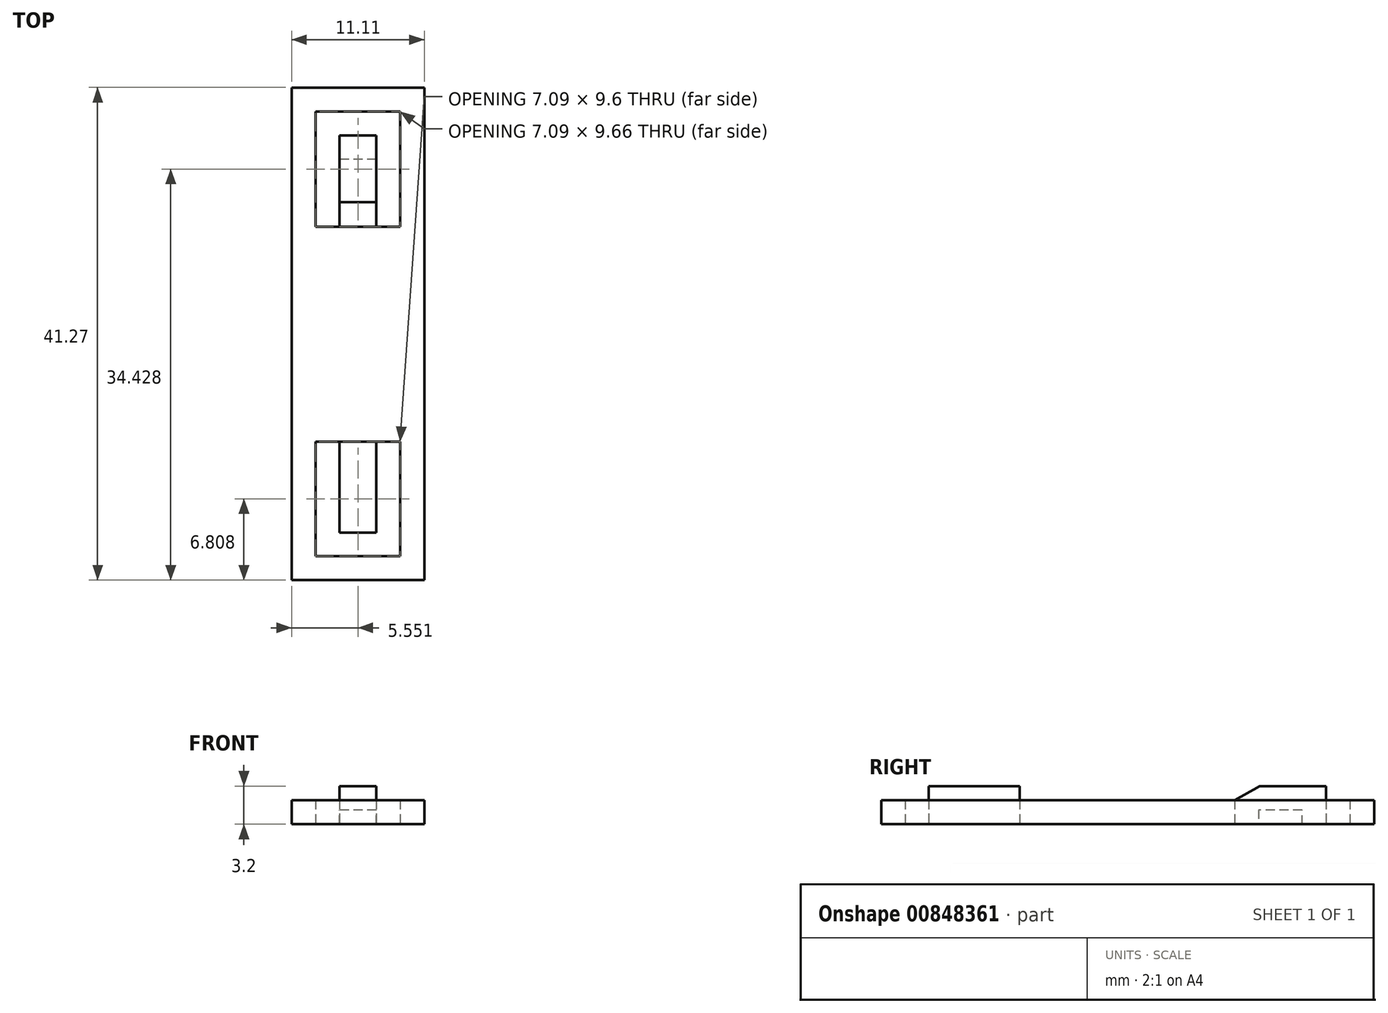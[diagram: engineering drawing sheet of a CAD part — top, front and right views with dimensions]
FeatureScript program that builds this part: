
annotation { "Feature Type Name" : "Feature", "Feature Type Description" : "" }
export const myFeature = defineFeature(function(context is Context, id is Id, definition is map)
    precondition{}
    {
        {
            var Q0;
            Q0=qCreatedBy(makeId("Top.planeOp"),FACE);
            var sketch = newSketch(context, id + "F0", { "sketchPlane" : qUnion([Q0])});
            skLineSegment(sketch, "E0.bottom", {"start": v(-36.94, 49.62) * mm, "end": v(-29.85, 49.62) * mm});
            skLineSegment(sketch, "E0.top", {"start": v(-36.94, 39.96) * mm, "end": v(-34.94, 39.96) * mm});
            skLineSegment(sketch, "E0.left", {"start": v(-36.94, 49.62) * mm, "end": v(-36.94, 39.96) * mm});
            skLineSegment(sketch, "E0.right", {"start": v(-29.85, 49.62) * mm, "end": v(-29.85, 39.96) * mm});
            skLineSegment(sketch, "E1.top", {"start": v(-34.94, 47.61) * mm, "end": v(-31.86, 47.61) * mm});
            skLineSegment(sketch, "E1.left", {"start": v(-34.94, 39.96) * mm, "end": v(-34.94, 47.61) * mm});
            skLineSegment(sketch, "E1.right", {"start": v(-31.86, 39.96) * mm, "end": v(-31.86, 47.61) * mm});
            skLineSegment(sketch, "E2.MirrorCS", {"start": v(-36.94, 12.34) * mm, "end": v(-36.94, 21.97) * mm});
            skLineSegment(sketch, "E3.MirrorCS", {"start": v(-36.94, 12.37) * mm, "end": v(-29.85, 12.37) * mm});
            skLineSegment(sketch, "E4.MirrorCS", {"start": v(-34.94, 14.35) * mm, "end": v(-31.86, 14.35) * mm});
            skLineSegment(sketch, "E5.MirrorCS", {"start": v(-34.94, 21.97) * mm, "end": v(-34.94, 14.35) * mm});
            skLineSegment(sketch, "E6.MirrorCS", {"start": v(-36.94, 21.97) * mm, "end": v(-34.94, 21.97) * mm});
            skLineSegment(sketch, "E7.MirrorCS", {"start": v(-29.85, 12.34) * mm, "end": v(-29.85, 21.97) * mm});
            skLineSegment(sketch, "E8.MirrorCS", {"start": v(-31.86, 21.97) * mm, "end": v(-31.86, 14.35) * mm});
            skLineSegment(sketch, "E9.trimOffspring", {"start": v(-31.86, 39.96) * mm, "end": v(-29.85, 39.96) * mm});
            skLineSegment(sketch, "E10.trimOffspring", {"start": v(-31.86, 21.97) * mm, "end": v(-29.85, 21.97) * mm});
            skLineSegment(sketch, "E11.bottom", {"start": v(-38.95, 51.63) * mm, "end": v(-27.84, 51.63) * mm});
            skLineSegment(sketch, "E11.top", {"start": v(-38.95, 10.36) * mm, "end": v(-33.4, 10.36) * mm});
            skLineSegment(sketch, "E11.left", {"start": v(-38.95, 51.63) * mm, "end": v(-38.95, 10.36) * mm});
            skLineSegment(sketch, "E11.right", {"start": v(-27.84, 51.63) * mm, "end": v(-27.84, 10.36) * mm});
            skLineSegment(sketch, "E12", {"start": v(-33.4, 51.63) * mm, "end": v(-33.4, 10.36) * mm, "construction": true});
            skLineSegment(sketch, "E13", {"start": v(-38.95, 31) * mm, "end": v(-27.84, 31) * mm, "construction": true});
            skLineSegment(sketch, "E14.trimOffspring", {"start": v(-33.4, 10.36) * mm, "end": v(-27.84, 10.36) * mm});
            skLineSegment(sketch, "E15", {"start": v(-34.94, 39.96) * mm, "end": v(-31.86, 39.96) * mm});
            skLineSegment(sketch, "E16", {"start": v(-34.94, 21.97) * mm, "end": v(-31.86, 21.97) * mm});
            skSolve(sketch);
        }
        {
            var Q0;
            Q0=qSketchRegion(id+"F0",true);
            var Q1;
            Q1=makeQuery(id+"F0.imprint","IMPRINT",FACE,{"disambiguationData":[TD([[makeQuery(id+"F0.imprint","IMPRINT",EDGE,{"derivedFrom":sQuery(id+"F0.wireOp",EDGE,"E4.MirrorCS")}),1.0]])]});
            var Q2;
            Q2=makeQuery(id+"F0.imprint","IMPRINT",FACE,{"disambiguationData":[TD([[makeQuery(id+"F0.imprint","IMPRINT",EDGE,{"derivedFrom":sQuery(id+"F0.wireOp",EDGE,"E1.top")}),-1.0]])]});
            extrude(context, id + "F1", {"entities" : qUnion([Q0, Q1, Q2]), "depth" : 2 * mm, "offsetDistance" : 25 * mm});
        }
        {
            var Q0;
            Q0=makeQuery(id+"F0.imprint","IMPRINT",FACE,{"disambiguationData":[TD([[makeQuery(id+"F0.imprint","IMPRINT",EDGE,{"derivedFrom":sQuery(id+"F0.wireOp",EDGE,"E1.top")}),-1.0]])]});
            var Q1;
            Q1=makeQuery(id+"F0.imprint","IMPRINT",FACE,{"disambiguationData":[TD([[makeQuery(id+"F0.imprint","IMPRINT",EDGE,{"derivedFrom":sQuery(id+"F0.wireOp",EDGE,"E4.MirrorCS")}),1.0]])]});
            extrude(context, id + "F2", {"entities" : qUnion([Q0, Q1]), "operationType" : NewBodyOperationType.ADD, "depth" : 3.2 * mm, "offsetDistance" : 25 * mm});
        }
        {
            var Q0;
            {var subQ0=sQuery(id+"F0.wireOp",EDGE,"E1.left");Q0=makeQuery(id+"F2.boolean.opBoolean","MERGE",FACE,{"derivedFrom":[makeQuery(id+"F1.opExtrude","SWEPT_FACE",FACE,{"disambiguationData":[OSD([subQ0])]}),makeQuery(id+"F2.opExtrude","SWEPT_FACE",FACE,{"disambiguationData":[OSD([subQ0])]})]});}
            var sketch = newSketch(context, id + "F3", { "sketchPlane" : qUnion([Q0])});
            skLineSegment(sketch, "E17", {"start": v(-45.61, 0) * mm, "end": v(-45.61, 1.2) * mm});
            skLineSegment(sketch, "E18", {"start": v(-45.61, 1.2) * mm, "end": v(-41.96, 1.2) * mm});
            skLineSegment(sketch, "E19", {"start": v(-41.96, 1.2) * mm, "end": v(-41.96, 0) * mm});
            skLineSegment(sketch, "E20", {"start": v(-39.96, 2) * mm, "end": v(-42.04, 3.2) * mm});
            skSolve(sketch);
        }
        {
            var Q0;
            {var subQ0=sQuery(id+"F3.wireOp",EDGE,"E17");Q0=makeQuery(id+"F3.imprint","IMPRINT",FACE,{"disambiguationData":[TD([[makeQuery(id+"F3.imprint","IMPRINT",EDGE,{"derivedFrom":subQ0}),-1.0]])]});}
            extrude(context, id + "F4", {"entities" : qUnion([Q0]), "operationType" : NewBodyOperationType.REMOVE, "endBound" : BoundingType.UP_TO_NEXT, "oppositeDirection" : true, "depth" : 25 * mm, "offsetDistance" : 25 * mm});
        }
        {
            var Q0;
            {var subQ0=sQuery(id+"F3.wireOp",EDGE,"E20");Q0=makeQuery(id+"F3.imprint","IMPRINT",FACE,{"disambiguationData":[TD([[makeQuery(id+"F3.imprint","IMPRINT",EDGE,{"derivedFrom":subQ0}),-1.0]])]});}
            extrude(context, id + "F5", {"entities" : qUnion([Q0]), "operationType" : NewBodyOperationType.REMOVE, "oppositeDirection" : true, "depth" : 25 * mm, "offsetDistance" : 25 * mm});
        }
    });
